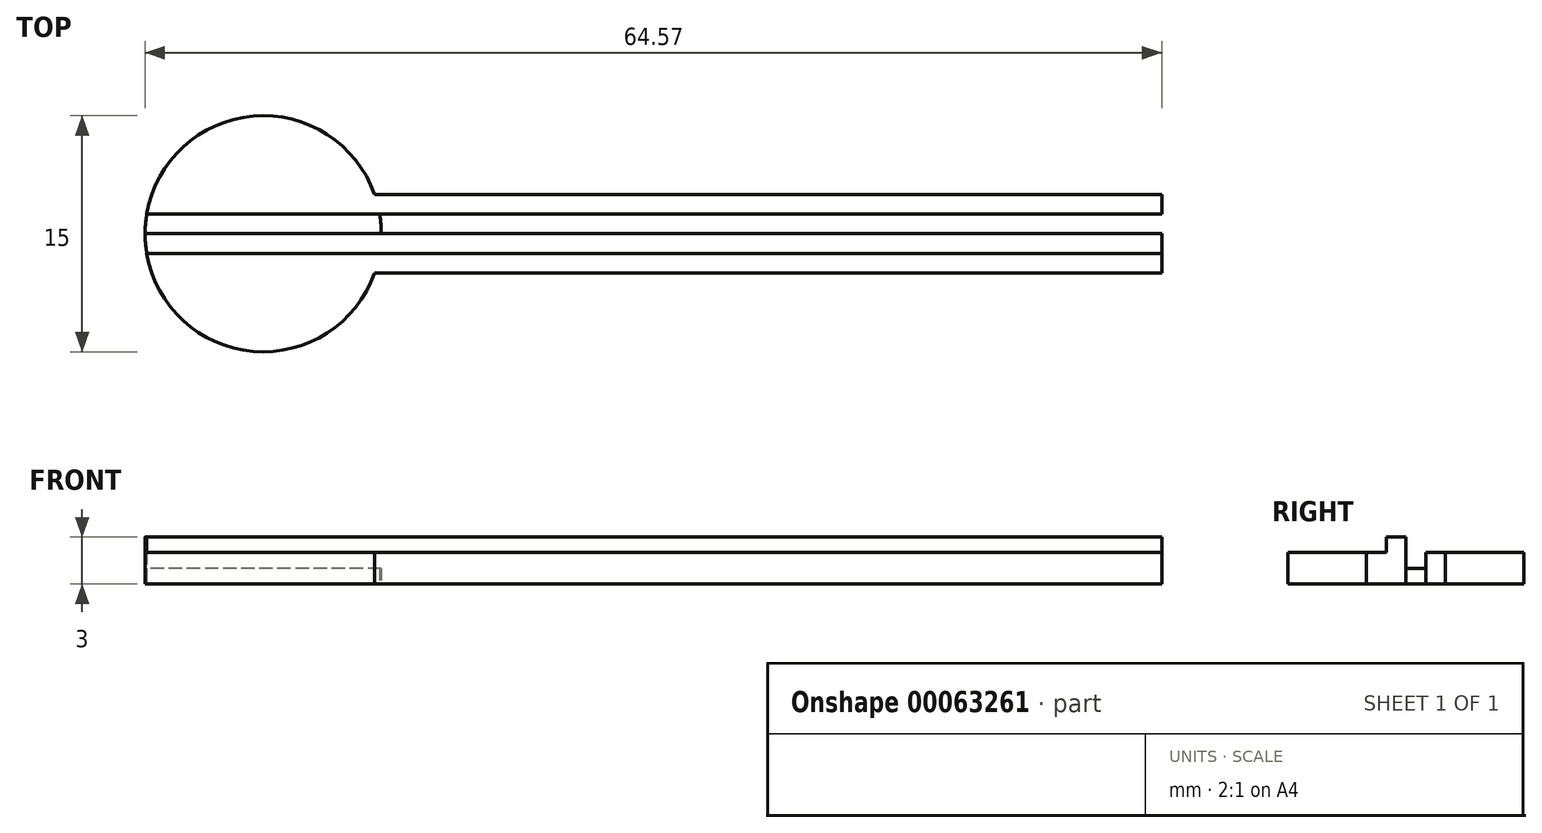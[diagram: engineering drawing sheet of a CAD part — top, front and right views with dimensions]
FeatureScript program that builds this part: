
annotation { "Feature Type Name" : "Feature", "Feature Type Description" : "" }
export const myFeature = defineFeature(function(context is Context, id is Id, definition is map)
    precondition{}
    {
        {
            var Q0;
            Q0=qCreatedBy(makeId("Top.planeOp"),FACE);
            var sketch = newSketch(context, id + "F0", { "sketchPlane" : qUnion([Q0])});
            skLineSegment(sketch, "E0.top", {"start": v(-60.05, 27.64) * mm, "end": v(-10.05, 27.64) * mm});
            skCircle(sketch, "E1", {"center": v(-67.12, 30.14) * mm, "radius": 7.5 * mm});
            skLineSegment(sketch, "E2.MirrorCS", {"start": v(-59.62, 30.14) * mm, "end": v(-10.05, 30.14) * mm});
            skLineSegment(sketch, "E3", {"start": v(-10.05, 27.64) * mm, "end": v(-10.05, 30.14) * mm});
            skLineSegment(sketch, "E4.MirrorCS", {"start": v(-60.05, 32.64) * mm, "end": v(-10.05, 32.64) * mm});
            skLineSegment(sketch, "E5.MirrorCS", {"start": v(-10.05, 32.64) * mm, "end": v(-10.05, 30.14) * mm});
            skPoint(sketch, "E6.oppositeSnap0", {"position": v(-10.05, 31.4) * mm});
            skLineSegment(sketch, "E6.bottom", {"start": v(-10.05, 30.14) * mm, "end": v(-74.62, 30.14) * mm});
            skLineSegment(sketch, "E6.top", {"start": v(-10.05, 31.4) * mm, "end": v(-74.52, 31.4) * mm});
            skLineSegment(sketch, "E6.left", {"start": v(-10.05, 30.14) * mm, "end": v(-10.05, 31.4) * mm});
            skLineSegment(sketch, "E7.MirrorCS", {"start": v(-10.05, 28.9) * mm, "end": v(-74.52, 28.9) * mm});
            skSolve(sketch);
        }
        {
            var Q0;
            {var subQ0=sQuery(id+"F0.wireOp",EDGE,"E0.top");Q0=makeQuery(id+"F0.imprint","IMPRINT",FACE,{"disambiguationData":[TD([[makeQuery(id+"F0.imprint","IMPRINT",EDGE,{"derivedFrom":subQ0}),1.0]])]});}
            var Q1;
            {var subQ0=sQuery(id+"F0.wireOp",EDGE,"E1");var subQ1=makeQuery(id+"F0.imprint","INTERSECT",VERTEX,{"derivedFrom":[subQ0,sQuery(id+"F0.wireOp",EDGE,"E4.MirrorCS")]});Q1=makeQuery(id+"F0.imprint","IMPRINT",FACE,{"disambiguationData":[TD([[makeQuery(id+"F0.imprint","IMPRINT",EDGE,{"disambiguationData":[TD([[subQ1,1.0]])],"derivedFrom":subQ0}),1.0]])]});}
            var Q2;
            {var subQ0=sQuery(id+"F0.wireOp",EDGE,"E4.MirrorCS");Q2=makeQuery(id+"F0.imprint","IMPRINT",FACE,{"disambiguationData":[TD([[makeQuery(id+"F0.imprint","IMPRINT",EDGE,{"derivedFrom":subQ0}),-1.0]])]});}
            var Q3;
            {var subQ0=sQuery(id+"F0.wireOp",EDGE,"E1");var subQ1=makeQuery(id+"F0.imprint","INTERSECT",VERTEX,{"derivedFrom":[sQuery(id+"F0.wireOp",EDGE,"E0.top"),subQ0]});Q3=makeQuery(id+"F0.imprint","IMPRINT",FACE,{"disambiguationData":[TD([[makeQuery(id+"F0.imprint","IMPRINT",EDGE,{"disambiguationData":[TD([[subQ1,1.0]])],"derivedFrom":subQ0}),1.0]])]});}
            extrude(context, id + "F1", {"entities" : qUnion([Q0, Q1, Q2, Q3]), "depth" : 2 * mm});
        }
        {
            var Q0;
            {var subQ0=sQuery(id+"F0.wireOp",EDGE,"E6.bottom");var subQ1=sQuery(id+"F0.wireOp",EDGE,"E1");var subQ2=makeQuery(id+"F0.imprint","INTERSECT",VERTEX,{"disambiguationData":[OD(0.0)],"derivedFrom":[subQ1,subQ0]});Q0=makeQuery(id+"F0.imprint","IMPRINT",FACE,{"disambiguationData":[TD([[makeQuery(id+"F0.imprint","IMPRINT",EDGE,{"disambiguationData":[TD([[subQ2,-1.0]])],"derivedFrom":subQ1}),1.0]])]});}
            var Q1;
            {var subQ0=sQuery(id+"F0.wireOp",EDGE,"E7.MirrorCS");var subQ1=sQuery(id+"F0.wireOp",EDGE,"E1");var subQ2=makeQuery(id+"F0.imprint","INTERSECT",VERTEX,{"disambiguationData":[OD(1.0)],"derivedFrom":[subQ1,subQ0]});Q1=makeQuery(id+"F0.imprint","IMPRINT",FACE,{"disambiguationData":[TD([[makeQuery(id+"F0.imprint","IMPRINT",EDGE,{"disambiguationData":[TD([[subQ2,-1.0]])],"derivedFrom":subQ1}),-1.0]])]});}
            extrude(context, id + "F2", {"entities" : qUnion([Q0, Q1]), "operationType" : NewBodyOperationType.ADD, "depth" : 3 * mm});
        }
        {
            var Q0;
            {var subQ0=sQuery(id+"F0.wireOp",EDGE,"E6.bottom");var subQ1=sQuery(id+"F0.wireOp",EDGE,"E1");var subQ2=makeQuery(id+"F0.imprint","INTERSECT",VERTEX,{"disambiguationData":[OD(0.0)],"derivedFrom":[subQ1,subQ0]});Q0=makeQuery(id+"F0.imprint","IMPRINT",FACE,{"disambiguationData":[TD([[makeQuery(id+"F0.imprint","IMPRINT",EDGE,{"disambiguationData":[TD([[subQ2,1.0]])],"derivedFrom":subQ1}),1.0]])]});}
            var Q1;
            {var subQ5=sQuery(id+"F0.wireOp",EDGE,"E6.left");Q1=makeQuery(id+"F0.imprint","IMPRINT",FACE,{"disambiguationData":[TD([[makeQuery(id+"F0.imprint","IMPRINT",EDGE,{"derivedFrom":subQ5}),1.0]])]});}
            extrude(context, id + "F3", {"entities" : qUnion([Q0, Q1]), "depth" : 1 * mm});
        }
    });
